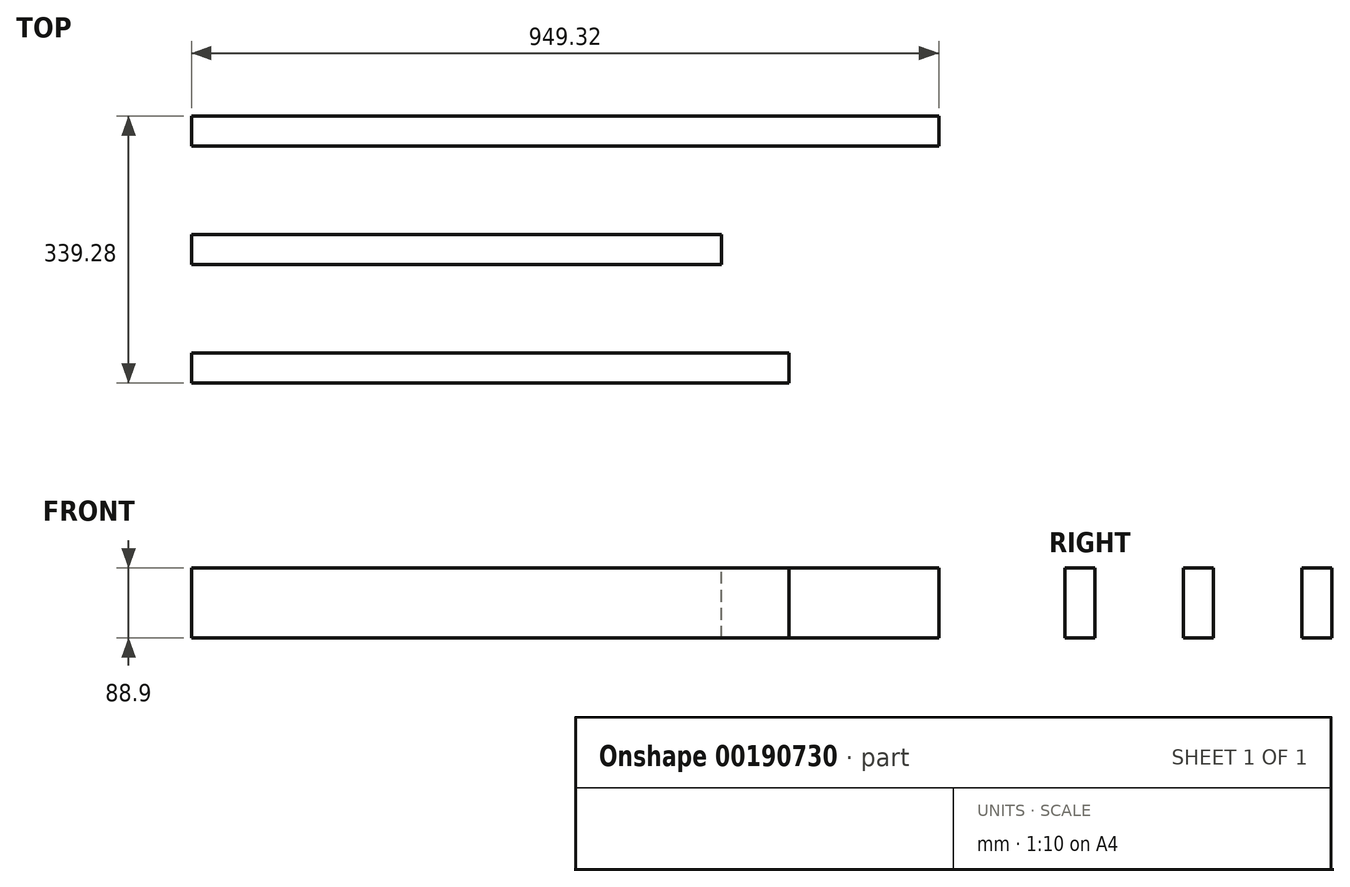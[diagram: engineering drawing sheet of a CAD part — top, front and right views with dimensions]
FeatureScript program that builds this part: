
annotation { "Feature Type Name" : "Feature", "Feature Type Description" : "" }
export const myFeature = defineFeature(function(context is Context, id is Id, definition is map)
    precondition{}
    {
        {
            var Q0;
            Q0=qCreatedBy(makeId("Right.planeOp"),FACE);
            var sketch = newSketch(context, id + "F0", { "sketchPlane" : qUnion([Q0])});
            skLineSegment(sketch, "E0.bottom", {"start": v(0, 0) * mm, "end": v(38.1, 0) * mm});
            skLineSegment(sketch, "E0.top", {"start": v(0, 88.9) * mm, "end": v(38.1, 88.9) * mm});
            skLineSegment(sketch, "E0.left", {"start": v(0, 0) * mm, "end": v(0, 88.9) * mm});
            skLineSegment(sketch, "E0.right", {"start": v(38.1, 0) * mm, "end": v(38.1, 88.9) * mm});
            skSolve(sketch);
        }
        {
            var Q0;
            Q0 = qSketchRegion(id + "F0", true);
            extrude(context, id + "F1", {"entities" : qUnion([Q0]), "depth" : 949.32 * mm});
        }
        {
            var Q0;
            Q0=qCreatedBy(makeId("Right.planeOp"),FACE);
            var sketch = newSketch(context, id + "F2", { "sketchPlane" : qUnion([Q0])});
            skLineSegment(sketch, "E1.bottom", {"start": v(-150.68, 0) * mm, "end": v(-112.58, 0) * mm});
            skLineSegment(sketch, "E1.top", {"start": v(-150.68, 88.9) * mm, "end": v(-112.58, 88.9) * mm});
            skLineSegment(sketch, "E1.left", {"start": v(-150.68, 0) * mm, "end": v(-150.68, 88.9) * mm});
            skLineSegment(sketch, "E1.right", {"start": v(-112.58, 0) * mm, "end": v(-112.58, 88.9) * mm});
            skSolve(sketch);
        }
        {
            var Q0;
            Q0 = qSketchRegion(id + "F2", true);
            extrude(context, id + "F3", {"entities" : qUnion([Q0]), "depth" : 673.1 * mm});
        }
        {
            var Q0;
            Q0=qCreatedBy(makeId("Right.planeOp"),FACE);
            var sketch = newSketch(context, id + "F4", { "sketchPlane" : qUnion([Q0])});
            skLineSegment(sketch, "E2.bottom", {"start": v(-301.18, 0) * mm, "end": v(-263.08, 0) * mm});
            skLineSegment(sketch, "E2.top", {"start": v(-301.18, 88.9) * mm, "end": v(-263.08, 88.9) * mm});
            skLineSegment(sketch, "E2.left", {"start": v(-301.18, 0) * mm, "end": v(-301.18, 88.9) * mm});
            skLineSegment(sketch, "E2.right", {"start": v(-263.08, 0) * mm, "end": v(-263.08, 88.9) * mm});
            skSolve(sketch);
        }
        {
            var Q0;
            Q0 = qSketchRegion(id + "F4", true);
            extrude(context, id + "F5", {"entities" : qUnion([Q0]), "depth" : 758.82 * mm});
        }
    });
